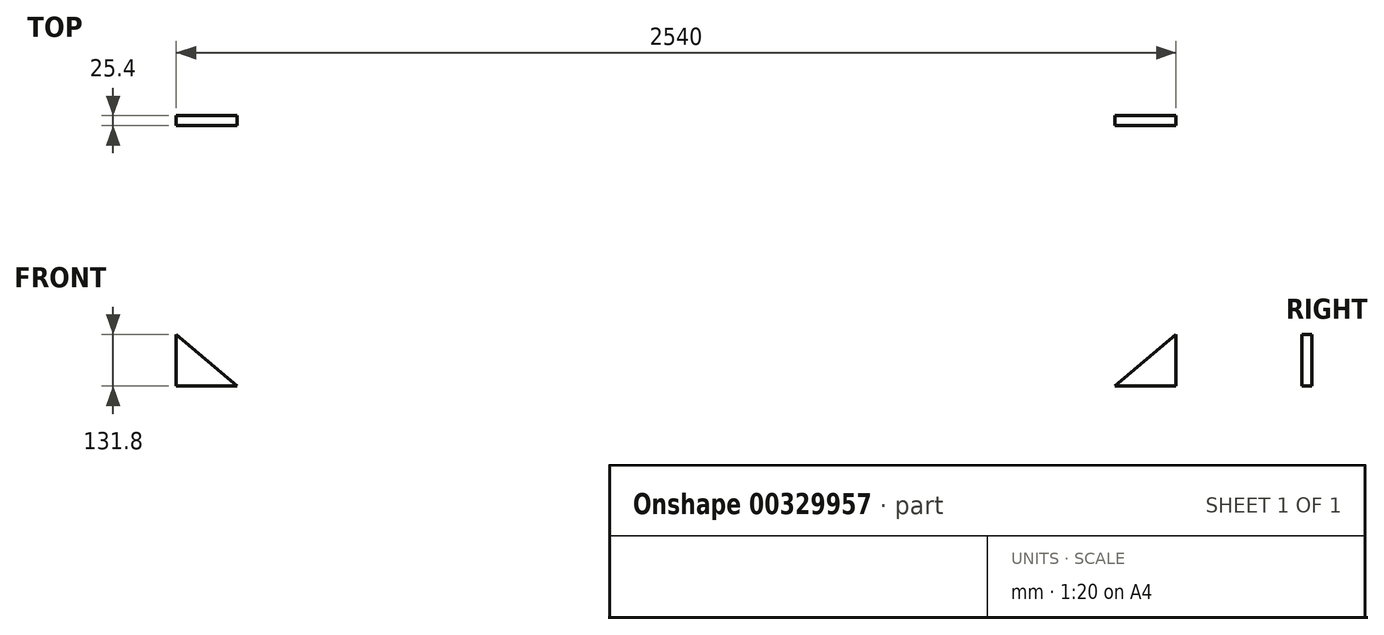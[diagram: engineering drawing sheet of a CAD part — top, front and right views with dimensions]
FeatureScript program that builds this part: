
annotation { "Feature Type Name" : "Feature", "Feature Type Description" : "" }
export const myFeature = defineFeature(function(context is Context, id is Id, definition is map)
    precondition{}
    {
        {
            var Q0;
            Q0=qCreatedBy(makeId("Front.planeOp"),FACE);
            var sketch = newSketch(context, id + "F0", { "sketchPlane" : qUnion([Q0])});
            skLineSegment(sketch, "E0", {"start": v(-655.25, -131.8) * mm, "end": v(1884.75, -131.8) * mm});
            skLineSegment(sketch, "E1", {"start": v(1884.75, -131.8) * mm, "end": v(1884.75, 325.4) * mm});
            skLineSegment(sketch, "E2", {"start": v(1884.75, 325.4) * mm, "end": v(1884.75, 706.4) * mm});
            skLineSegment(sketch, "E3", {"start": v(1884.75, 706.4) * mm, "end": v(1884.75, 1112.8) * mm});
            skLineSegment(sketch, "E4", {"start": v(1884.75, 1112.8) * mm, "end": v(1884.75, 1417.6) * mm});
            skLineSegment(sketch, "E5", {"start": v(1884.75, 1417.6) * mm, "end": v(1884.75, 1722.4) * mm});
            skLineSegment(sketch, "E6", {"start": v(1884.75, 1722.4) * mm, "end": v(1275.15, 1722.4) * mm});
            skLineSegment(sketch, "E7", {"start": v(1275.15, 1722.4) * mm, "end": v(1275.15, 1417.6) * mm});
            skLineSegment(sketch, "E8", {"start": v(1275.15, 1417.6) * mm, "end": v(1275.15, 1112.8) * mm});
            skLineSegment(sketch, "E9", {"start": v(1275.15, 1112.8) * mm, "end": v(1884.75, 1112.8) * mm});
            skLineSegment(sketch, "E10", {"start": v(1275.15, 1417.6) * mm, "end": v(1884.75, 1417.6) * mm});
            skLineSegment(sketch, "E11", {"start": v(1884.75, 706.4) * mm, "end": v(360.75, 706.4) * mm});
            skLineSegment(sketch, "E12", {"start": v(360.75, 706.4) * mm, "end": v(360.75, -131.8) * mm});
            skLineSegment(sketch, "E13", {"start": v(-655.25, -131.8) * mm, "end": v(-655.25, 579.4) * mm});
            skLineSegment(sketch, "E14", {"start": v(1275.15, 1112.8) * mm, "end": v(360.75, 1112.8) * mm});
            skLineSegment(sketch, "E15", {"start": v(360.75, 1112.8) * mm, "end": v(360.75, 706.4) * mm});
            skLineSegment(sketch, "E16", {"start": v(1884.75, 325.4) * mm, "end": v(868.75, 325.4) * mm});
            skLineSegment(sketch, "E17.0", {"start": v(868.75, 706.4) * mm, "end": v(868.75, -131.8) * mm});
            skLineSegment(sketch, "E18", {"start": v(-655.25, 579.4) * mm, "end": v(-655.25, 782.6) * mm});
            skLineSegment(sketch, "E19", {"start": v(-655.25, 782.6) * mm, "end": v(-655.25, 1239.8) * mm});
            skLineSegment(sketch, "E20", {"start": v(1275.15, 1570) * mm, "end": v(817.95, 1570) * mm});
            skPoint(sketch, "E20.endSnap0", {"position": v(817.95, 1112.8) * mm});
            skLineSegment(sketch, "E21", {"start": v(817.95, 1570) * mm, "end": v(817.95, 1112.8) * mm});
            skLineSegment(sketch, "E22", {"start": v(817.95, 1341.4) * mm, "end": v(360.75, 1341.4) * mm});
            skLineSegment(sketch, "E23", {"start": v(360.75, 1341.4) * mm, "end": v(360.75, 1112.8) * mm});
            skLineSegment(sketch, "E24", {"start": v(1376.75, 706.4) * mm, "end": v(1376.75, 325.4) * mm});
            skPoint(sketch, "E24.startSnap0", {"position": v(1376.75, 325.4) * mm});
            skLineSegment(sketch, "E25", {"start": v(-655.25, 311.07) * mm, "end": v(360.75, 311.07) * mm});
            skLineSegment(sketch, "E26", {"start": v(-655.25, 782.6) * mm, "end": v(360.75, 782.6) * mm});
            skLineSegment(sketch, "E27", {"start": v(-655.25, 579.4) * mm, "end": v(360.75, 579.4) * mm});
            skLineSegment(sketch, "E28.0", {"start": v(-147.25, -131.8) * mm, "end": v(-147.25, 579.4) * mm});
            skLineSegment(sketch, "E29.0", {"start": v(-452.05, 579.4) * mm, "end": v(-452.05, 782.6) * mm});
            skLineSegment(sketch, "E30.0", {"start": v(-248.85, 579.4) * mm, "end": v(-248.85, 782.6) * mm});
            skLineSegment(sketch, "E31.0", {"start": v(-45.65, 579.4) * mm, "end": v(-45.65, 782.6) * mm});
            skLineSegment(sketch, "E32.0", {"start": v(157.55, 579.4) * mm, "end": v(157.55, 782.6) * mm});
            skLineSegment(sketch, "E33", {"start": v(-655.25, 1239.8) * mm, "end": v(-45.65, 1239.8) * mm});
            skLineSegment(sketch, "E34", {"start": v(-45.65, 1239.8) * mm, "end": v(-45.65, 782.6) * mm});
            skLineSegment(sketch, "E35", {"start": v(-350.45, 1239.8) * mm, "end": v(-350.45, 782.6) * mm});
            skLineSegment(sketch, "E36", {"start": v(1376.75, 325.4) * mm, "end": v(1376.75, -131.8) * mm});
            skLineSegment(sketch, "E37", {"start": v(1884.75, 0) * mm, "end": v(1730.1, -131.8) * mm});
            skPoint(sketch, "E37.startSnap0", {"position": v(1884.75, 96.8) * mm});
            skLineSegment(sketch, "E38", {"start": v(-655.25, 0) * mm, "end": v(-500.6, -131.8) * mm});
            skSolve(sketch);
        }
        {
            var Q0;
            Q0=sQuery(id+"F0.wireOp",EDGE,"E0");
            extrude(context, id + "F1", {"bodyType" : ToolBodyType.SURFACE, "surfaceEntities" : qUnion([Q0]), "depth" : 406.4 * mm});
        }
        {
            var Q0;
            Q0=sQuery(id+"F0.wireOp",EDGE,"E11");
            var Q1;
            Q1=sQuery(id+"F0.wireOp",EDGE,"E14");
            var Q2;
            Q2=sQuery(id+"F0.wireOp",EDGE,"E9");
            var Q3;
            Q3=sQuery(id+"F0.wireOp",EDGE,"E26");
            var Q4;
            Q4=sQuery(id+"F0.wireOp",EDGE,"E27");
            var Q5;
            Q5=sQuery(id+"F0.wireOp",EDGE,"E25");
            var Q6;
            Q6=sQuery(id+"F0.wireOp",EDGE,"rV22Ptz8-5m0V-YlpI-b4gg-Ob9M7tdslO94");
            var Q7;
            Q7=sQuery(id+"F0.wireOp",EDGE,"bKKIS1st-ZlHM-1BwP-y86K-tYbj4GIVGfuE");
            var Q8;
            Q8=sQuery(id+"F0.wireOp",EDGE,"E22");
            var Q9;
            Q9=sQuery(id+"F0.wireOp",EDGE,"E20");
            var Q10;
            Q10=sQuery(id+"F0.wireOp",EDGE,"E6");
            var Q11;
            Q11=sQuery(id+"F0.wireOp",EDGE,"E10");
            var Q12;
            Q12=sQuery(id+"F0.wireOp",EDGE,"E16");
            extrude(context, id + "F2", {"bodyType" : ToolBodyType.SURFACE, "surfaceEntities" : qUnion([Q0, Q1, Q2, Q3, Q4, Q5, Q6, Q7, Q8, Q9, Q10, Q11, Q12]), "depth" : 406.4 * mm});
        }
        {
            var Q0;
            Q0=sQuery(id+"F0.wireOp",EDGE,"E19");
            var Q1;
            Q1=sQuery(id+"F0.wireOp",EDGE,"f34ovu7u-qaRi-kmOb-FgM2-FXpkdGRddNws");
            var Q2;
            Q2=sQuery(id+"F0.wireOp",EDGE,"E23");
            var Q3;
            Q3=sQuery(id+"F0.wireOp",EDGE,"E15");
            var Q4;
            Q4=sQuery(id+"F0.wireOp",EDGE,"E8");
            var Q5;
            Q5=sQuery(id+"F0.wireOp",EDGE,"E7");
            var Q6;
            Q6=sQuery(id+"F0.wireOp",EDGE,"E21");
            var Q7;
            Q7=sQuery(id+"F0.wireOp",EDGE,"E4");
            var Q8;
            Q8=sQuery(id+"F0.wireOp",EDGE,"E5");
            var Q9;
            Q9=sQuery(id+"F0.wireOp",EDGE,"E3");
            var Q10;
            Q10=sQuery(id+"F0.wireOp",EDGE,"E2");
            var Q11;
            Q11=sQuery(id+"F0.wireOp",EDGE,"E1");
            var Q12;
            Q12=sQuery(id+"F0.wireOp",EDGE,"08a15322-a80d-4ad6-87fd-102c70ec6452.0");
            var Q13;
            Q13=sQuery(id+"F0.wireOp",EDGE,"E17.0");
            var Q14;
            Q14=sQuery(id+"F0.wireOp",EDGE,"E24");
            var Q15;
            Q15=sQuery(id+"F0.wireOp",EDGE,"E12");
            var Q16;
            Q16=sQuery(id+"F0.wireOp",EDGE,"E28.0");
            var Q17;
            Q17=sQuery(id+"F0.wireOp",EDGE,"E13");
            var Q18;
            Q18=sQuery(id+"F0.wireOp",EDGE,"E18");
            var Q19;
            Q19=sQuery(id+"F0.wireOp",EDGE,"E29.0");
            var Q20;
            Q20=sQuery(id+"F0.wireOp",EDGE,"E30.0");
            var Q21;
            Q21=sQuery(id+"F0.wireOp",EDGE,"E31.0");
            var Q22;
            Q22=sQuery(id+"F0.wireOp",EDGE,"E32.0");
            extrude(context, id + "F3", {"bodyType" : ToolBodyType.SURFACE, "surfaceEntities" : qUnion([Q0, Q1, Q2, Q3, Q4, Q5, Q6, Q7, Q8, Q9, Q10, Q11, Q12, Q13, Q14, Q15, Q16, Q17, Q18, Q19, Q20, Q21, Q22]), "depth" : 406.4 * mm});
        }
        {
            var Q0;
            Q0=sQuery(id+"F0.wireOp",EDGE,"rV22Ptz8-5m0V-YlpI-b4gg-Ob9M7tdslO94");
            var Q1;
            Q1=sQuery(id+"F0.wireOp",EDGE,"bKKIS1st-ZlHM-1BwP-y86K-tYbj4GIVGfuE");
            var Q2;
            Q2=sQuery(id+"F0.wireOp",EDGE,"E19");
            var Q3;
            Q3=sQuery(id+"F0.wireOp",EDGE,"E14");
            var Q4;
            Q4=sQuery(id+"F0.wireOp",EDGE,"f34ovu7u-qaRi-kmOb-FgM2-FXpkdGRddNws");
            var Q5;
            Q5=sQuery(id+"F0.wireOp",EDGE,"E18");
            var Q6;
            Q6=sQuery(id+"F0.wireOp",EDGE,"E29.0");
            var Q7;
            Q7=sQuery(id+"F0.wireOp",EDGE,"E12");
            var Q8;
            Q8=sQuery(id+"F0.wireOp",EDGE,"E15");
            var Q9;
            Q9=sQuery(id+"F0.wireOp",EDGE,"E17.0");
            var Q10;
            Q10=sQuery(id+"F0.wireOp",EDGE,"E24");
            var Q11;
            Q11=sQuery(id+"F0.wireOp",EDGE,"08a15322-a80d-4ad6-87fd-102c70ec6452.0");
            var Q12;
            Q12=sQuery(id+"F0.wireOp",EDGE,"E6");
            var Q13;
            Q13=sQuery(id+"F0.wireOp",EDGE,"E5");
            var Q14;
            Q14=sQuery(id+"F0.wireOp",EDGE,"E4");
            var Q15;
            Q15=sQuery(id+"F0.wireOp",EDGE,"E3");
            var Q16;
            Q16=sQuery(id+"F0.wireOp",EDGE,"E2");
            var Q17;
            Q17=sQuery(id+"F0.wireOp",EDGE,"E1");
            var Q18;
            Q18=sQuery(id+"F0.wireOp",EDGE,"E7");
            var Q19;
            Q19=sQuery(id+"F0.wireOp",EDGE,"E8");
            extrude(context, id + "F4", {"bodyType" : ToolBodyType.SURFACE, "surfaceEntities" : qUnion([Q0, Q1, Q2, Q3, Q4, Q5, Q6, Q7, Q8, Q9, Q10, Q11, Q12, Q13, Q14, Q15, Q16, Q17, Q18, Q19]), "depth" : 406.4 * mm});
        }
        {
            var Q0;
            Q0=sQuery(id+"F0.wireOp",EDGE,"E33");
            extrude(context, id + "F5", {"bodyType" : ToolBodyType.SURFACE, "surfaceEntities" : qUnion([Q0]), "depth" : 406.4 * mm});
        }
        {
            var Q0;
            Q0=sQuery(id+"F0.wireOp",EDGE,"E35");
            var Q1;
            Q1=sQuery(id+"F0.wireOp",EDGE,"E34");
            var Q2;
            Q2=sQuery(id+"F0.wireOp",EDGE,"E36");
            extrude(context, id + "F6", {"bodyType" : ToolBodyType.SURFACE, "surfaceEntities" : qUnion([Q0, Q1, Q2]), "depth" : 406.4 * mm});
        }
        {
            var Q0;
            {var subQ3=sQuery(id+"F0.wireOp",EDGE,"E37");Q0=makeQuery(id+"F0.imprint","IMPRINT",FACE,{"disambiguationData":[TD([[makeQuery(id+"F0.imprint","IMPRINT",EDGE,{"derivedFrom":subQ3}),1.0]])]});}
            extrude(context, id + "F7", {"entities" : qUnion([Q0]), "depth" : 25.4 * mm});
        }
        {
            var Q0;
            {var subQ3=sQuery(id+"F0.wireOp",EDGE,"E38");Q0=makeQuery(id+"F0.imprint","IMPRINT",FACE,{"disambiguationData":[TD([[makeQuery(id+"F0.imprint","IMPRINT",EDGE,{"derivedFrom":subQ3}),-1.0]])]});}
            extrude(context, id + "F8", {"entities" : qUnion([Q0]), "depth" : 25.4 * mm});
        }
    });
